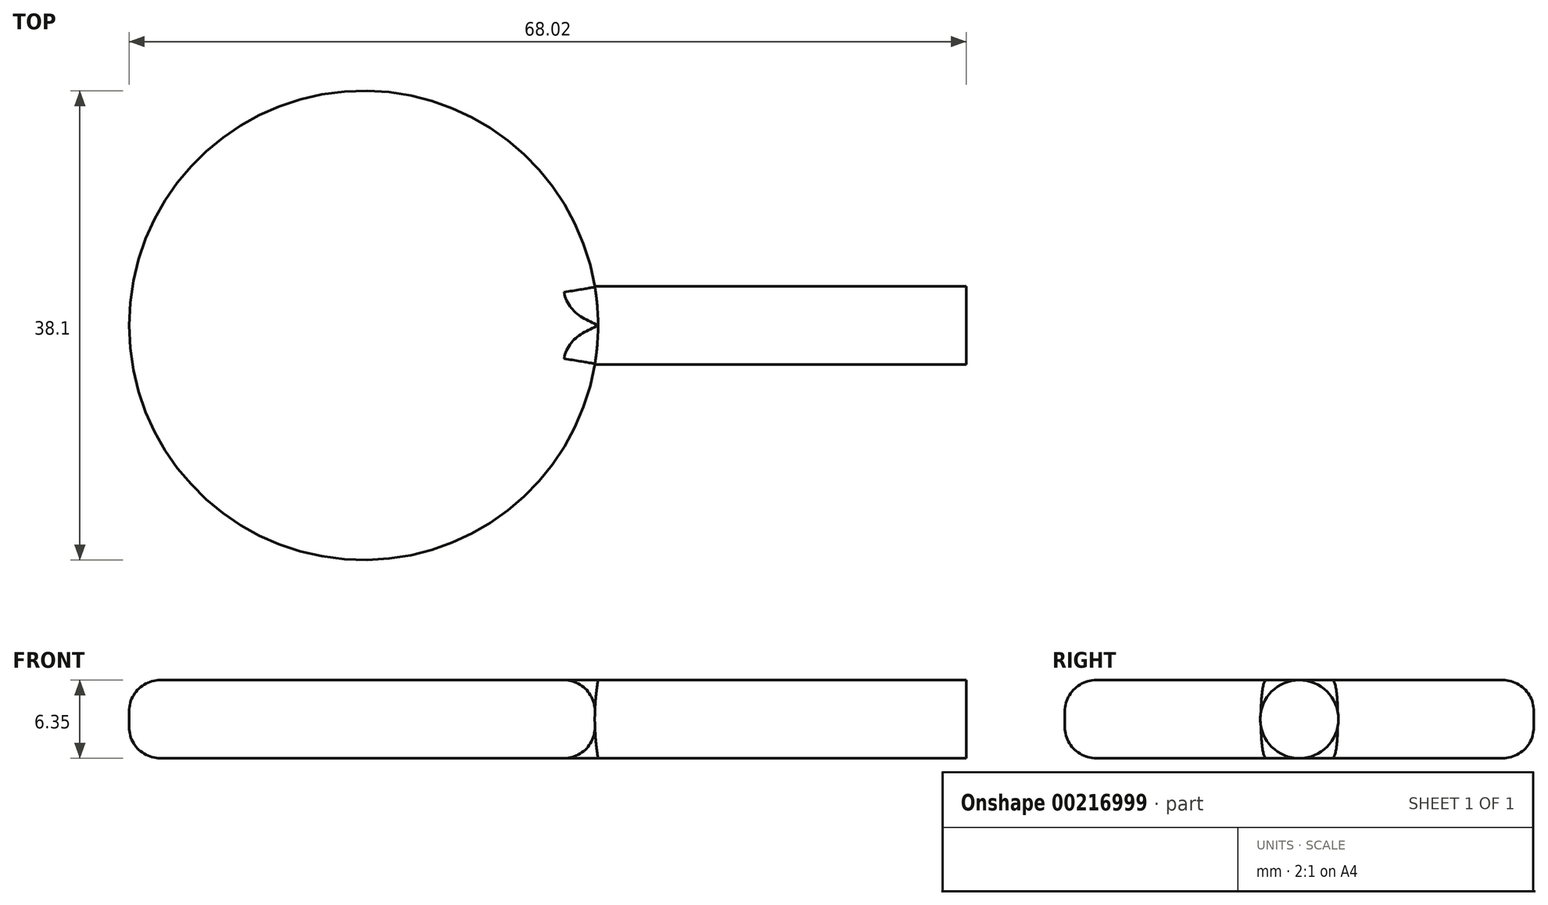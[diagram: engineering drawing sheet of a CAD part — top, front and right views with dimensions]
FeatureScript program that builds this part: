
annotation { "Feature Type Name" : "Feature", "Feature Type Description" : "" }
export const myFeature = defineFeature(function(context is Context, id is Id, definition is map)
    precondition{}
    {
        {
            var Q0;
            Q0=qCreatedBy(makeId("Top.planeOp"),FACE);
            var sketch = newSketch(context, id + "F0", { "sketchPlane" : qUnion([Q0])});
            skCircle(sketch, "E0", {"center": v(0, 0) * mm, "radius": 19.05 * mm});
            skLineSegment(sketch, "E1.bottom", {"start": v(48.97, -3.17) * mm, "end": v(18.78, -3.17) * mm});
            skLineSegment(sketch, "E1.top", {"start": v(48.97, 3.18) * mm, "end": v(18.78, 3.18) * mm});
            skLineSegment(sketch, "E1.left", {"start": v(48.97, -3.17) * mm, "end": v(48.97, 3.18) * mm});
            skPoint(sketch, "E1.right.end.orphan", {"position": v(-48.97, 3.17) * mm});
            skPoint(sketch, "E1.right.start.orphan", {"position": v(-48.97, -3.18) * mm});
            skSolve(sketch);
        }
        {
            var Q0;
            Q0 = qSketchRegion(id + "F0", true);
            extrude(context, id + "F1", {"entities" : qUnion([Q0]), "depth" : 6.35 * mm});
        }
        {
            var Q0;
            Q0=makeQuery(id+"F1.opExtrude","CAP_EDGE",EDGE,{"disambiguationData":[OSD([sQuery(id+"F0.wireOp",EDGE,"E1.bottom")])],"isStart":false});
            var Q1;
            Q1=makeQuery(id+"F1.opExtrude","CAP_EDGE",EDGE,{"disambiguationData":[OSD([sQuery(id+"F0.wireOp",EDGE,"E1.top")])],"isStart":false});
            var Q2;
            Q2=makeQuery(id+"F1.opExtrude","CAP_EDGE",EDGE,{"disambiguationData":[OSD([sQuery(id+"F0.wireOp",EDGE,"E1.bottom")])],"isStart":true});
            var Q3;
            Q3=makeQuery(id+"F1.opExtrude","CAP_EDGE",EDGE,{"disambiguationData":[OSD([sQuery(id+"F0.wireOp",EDGE,"E1.top")])],"isStart":true});
            fillet(context, id + "F2", {"entities" : qUnion([Q0, Q1, Q2, Q3]), "radius" : 3.17 * mm, "tangentPropagation" : true, "allowEdgeOverflow" : false});
        }
        {
            var Q0;
            Q0=makeQuery(id+"F1.opExtrude","CAP_EDGE",EDGE,{"disambiguationData":[OSD([sQuery(id+"F0.wireOp",EDGE,"E0")])],"isStart":true});
            var Q1;
            Q1=makeQuery(id+"F1.opExtrude","CAP_FACE",FACE,{"disambiguationData":[OSD([sQuery(id+"F0.wireOp",EDGE,"E0"),sQuery(id+"F0.wireOp",EDGE,"E1.bottom"),sQuery(id+"F0.wireOp",EDGE,"E1.top"),sQuery(id+"F0.wireOp",EDGE,"E1.left")])],"isStart":false});
            fillet(context, id + "F3", {"entities" : qUnion([Q0, Q1]), "radius" : 2.54 * mm, "tangentPropagation" : true, "allowEdgeOverflow" : false});
        }
    });
